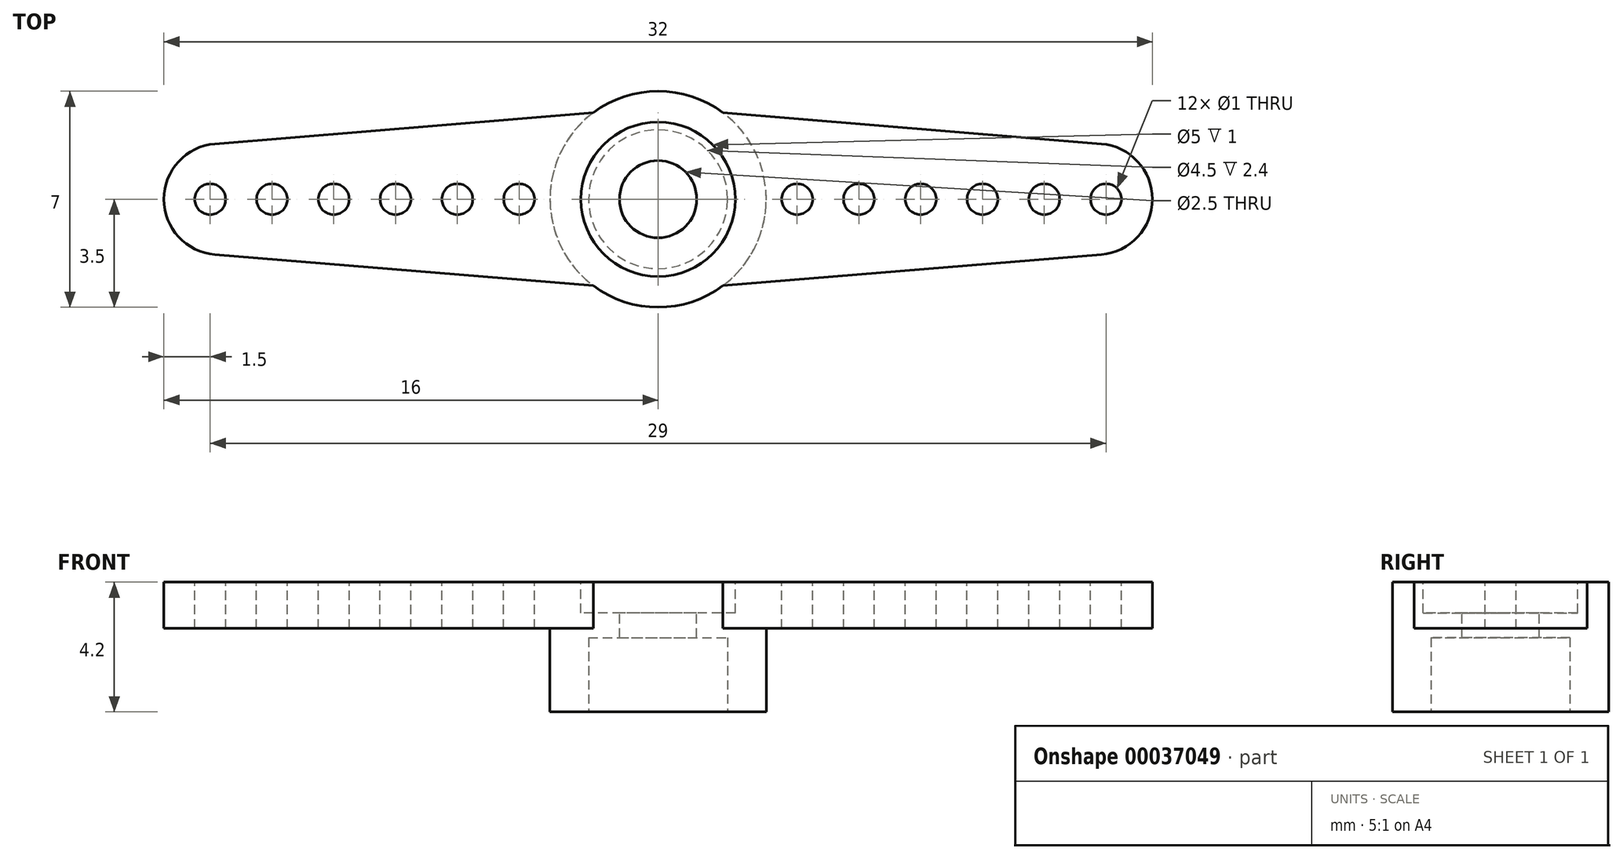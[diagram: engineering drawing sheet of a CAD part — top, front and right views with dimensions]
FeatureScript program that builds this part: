
annotation { "Feature Type Name" : "Feature", "Feature Type Description" : "" }
export const myFeature = defineFeature(function(context is Context, id is Id, definition is map)
    precondition{}
    {
        {
            var Q0;
            Q0=qCreatedBy(makeId("Top.planeOp"),FACE);
            var sketch = newSketch(context, id + "F0", { "sketchPlane" : qUnion([Q0])});
            skCircle(sketch, "E0", {"center": v(0, 0) * mm, "radius": 3.5 * mm});
            skCircle(sketch, "E1", {"center": v(0, 0) * mm, "radius": 16 * mm, "construction": true});
            skLineSegment(sketch, "E2", {"start": v(-16, 0) * mm, "end": v(16, 0) * mm, "construction": true});
            skArc(sketch, "E3", {"start": v(-14.35, 1.8) * mm, "mid": v(-16, 0) * mm, "end": v(-14.35, -1.8) * mm});
            skLineSegment(sketch, "E4", {"start": v(-14.35, 1.8) * mm, "end": v(-2.1, 2.8) * mm});
            skLineSegment(sketch, "E5.0.MirrorCS", {"start": v(-14.35, -1.8) * mm, "end": v(-2.1, -2.8) * mm});
            skLineSegment(sketch, "E6", {"start": v(0, 16) * mm, "end": v(0, -16) * mm, "construction": true});
            skLineSegment(sketch, "E7.0.MirrorCS", {"start": v(14.35, 1.8) * mm, "end": v(2.1, 2.8) * mm});
            skArc(sketch, "E8.0.MirrorCS", {"start": v(14.35, 1.8) * mm, "mid": v(16, 0) * mm, "end": v(14.35, -1.8) * mm});
            skLineSegment(sketch, "E9.0.MirrorCS", {"start": v(14.35, -1.8) * mm, "end": v(2.1, -2.8) * mm});
            skSolve(sketch);
        }
        {
            var Q0;
            {var subQ0=sQuery(id+"F0.wireOp",EDGE,"E0");var subQ4=makeQuery(id+"F0.imprint","INTERSECT",VERTEX,{"derivedFrom":[subQ0,sQuery(id+"F0.wireOp",EDGE,"E4")]});Q0=makeQuery(id+"F0.imprint","IMPRINT",FACE,{"disambiguationData":[TD([[makeQuery(id+"F0.imprint","IMPRINT",EDGE,{"disambiguationData":[TD([[subQ4,1.0]])],"derivedFrom":subQ0}),1.0]])]});}
            extrude(context, id + "F1", {"entities" : qUnion([Q0]), "depth" : 4.2 * mm});
        }
        {
            var Q0;
            Q0=makeQuery(id+"F1.opExtrude","CAP_FACE",FACE,{"disambiguationData":[OSD([sQuery(id+"F0.wireOp",EDGE,"E0")])],"isStart":false});
            var sketch = newSketch(context, id + "F2", { "sketchPlane" : qUnion([Q0])});
            skLineSegment(sketch, "E10.0", {"start": v(-14.35, 1.8) * mm, "end": v(-2.1, 2.8) * mm});
            skArc(sketch, "E11.0", {"start": v(-14.35, 1.8) * mm, "mid": v(-16, 0) * mm, "end": v(-14.35, -1.8) * mm});
            skLineSegment(sketch, "E12.0", {"start": v(-14.35, -1.8) * mm, "end": v(-2.1, -2.8) * mm});
            skLineSegment(sketch, "E13.0", {"start": v(14.35, -1.8) * mm, "end": v(2.1, -2.8) * mm});
            skArc(sketch, "E14.0", {"start": v(14.35, 1.8) * mm, "mid": v(16, 0) * mm, "end": v(14.35, -1.8) * mm});
            skLineSegment(sketch, "E15.0", {"start": v(14.35, 1.8) * mm, "end": v(2.1, 2.8) * mm});
            skArc(sketch, "E16.0", {"start": v(-2.1, 2.8) * mm, "mid": v(-3.5, 0) * mm, "end": v(-2.1, -2.8) * mm});
            skArc(sketch, "E17.trimOffspring", {"start": v(2.1, -2.8) * mm, "mid": v(3.5, 0) * mm, "end": v(2.1, 2.8) * mm});
            skLineSegment(sketch, "E18", {"start": v(-16, 0) * mm, "end": v(16, 0) * mm, "construction": true});
            skCircle(sketch, "E19", {"center": v(-14.5, 0) * mm, "radius": 0.5 * mm});
            skLineSegment(sketch, "E20", {"start": v(0, 4.57) * mm, "end": v(0, -5.46) * mm, "construction": true});
            skCircle(sketch, "E21.0.MirrorC", {"center": v(14.5, 0) * mm, "radius": 0.5 * mm});
            skCircle(sketch, "E22.1.0.0", {"center": v(-12.5, 0) * mm, "radius": 0.5 * mm});
            skCircle(sketch, "E22.2.0.0", {"center": v(-10.5, 0) * mm, "radius": 0.5 * mm});
            skCircle(sketch, "E22.3.0.0", {"center": v(-8.5, 0) * mm, "radius": 0.5 * mm});
            skCircle(sketch, "E22.4.0.0", {"center": v(-6.5, 0) * mm, "radius": 0.5 * mm});
            skCircle(sketch, "E22.5.0.0", {"center": v(-4.5, 0) * mm, "radius": 0.5 * mm});
            skLineSegment(sketch, "E22.direction1", {"start": v(-14.5, 0) * mm, "end": v(-12.5, 0) * mm, "construction": true});
            skCircle(sketch, "E23.0.MirrorC", {"center": v(4.5, 0) * mm, "radius": 0.5 * mm});
            skCircle(sketch, "E24.0.MirrorC", {"center": v(6.5, 0) * mm, "radius": 0.5 * mm});
            skCircle(sketch, "E25.0.MirrorC", {"center": v(8.5, 0) * mm, "radius": 0.5 * mm});
            skCircle(sketch, "E26.0.MirrorC", {"center": v(10.5, 0) * mm, "radius": 0.5 * mm});
            skCircle(sketch, "E27.0.MirrorC", {"center": v(12.5, 0) * mm, "radius": 0.5 * mm});
            skSolve(sketch);
        }
        {
            var Q0;
            Q0=qSketchRegion(id+"F2",true);
            extrude(context, id + "F3", {"entities" : qUnion([Q0]), "operationType" : NewBodyOperationType.ADD, "oppositeDirection" : true, "depth" : 1.5 * mm});
        }
        {
            var Q0;
            Q0=makeQuery(id+"F3.boolean.opBoolean","MERGE",FACE,{"derivedFrom":[makeQuery(id+"F1.opExtrude","CAP_FACE",FACE,{"disambiguationData":[OSD([sQuery(id+"F0.wireOp",EDGE,"E0")])],"isStart":false}),makeQuery(id+"F3.opExtrude","CAP_FACE",FACE,{"disambiguationData":[OSD([sQuery(id+"F2.wireOp",EDGE,"E10.0"),sQuery(id+"F2.wireOp",EDGE,"E11.0"),sQuery(id+"F2.wireOp",EDGE,"E12.0"),sQuery(id+"F2.wireOp",EDGE,"E16.0"),sQuery(id+"F2.wireOp",EDGE,"E19"),sQuery(id+"F2.wireOp",EDGE,"E22.1.0.0"),sQuery(id+"F2.wireOp",EDGE,"E22.2.0.0"),sQuery(id+"F2.wireOp",EDGE,"E22.3.0.0"),sQuery(id+"F2.wireOp",EDGE,"E22.4.0.0"),sQuery(id+"F2.wireOp",EDGE,"E22.5.0.0")])],"isStart":true}),makeQuery(id+"F3.opExtrude","CAP_FACE",FACE,{"disambiguationData":[OSD([sQuery(id+"F2.wireOp",EDGE,"E13.0"),sQuery(id+"F2.wireOp",EDGE,"E14.0"),sQuery(id+"F2.wireOp",EDGE,"E15.0"),sQuery(id+"F2.wireOp",EDGE,"E17.trimOffspring"),sQuery(id+"F2.wireOp",EDGE,"E21.0.MirrorC"),sQuery(id+"F2.wireOp",EDGE,"E23.0.MirrorC"),sQuery(id+"F2.wireOp",EDGE,"E24.0.MirrorC"),sQuery(id+"F2.wireOp",EDGE,"E25.0.MirrorC"),sQuery(id+"F2.wireOp",EDGE,"E26.0.MirrorC"),sQuery(id+"F2.wireOp",EDGE,"E27.0.MirrorC")])],"isStart":true})]});
            var sketch = newSketch(context, id + "F4", { "sketchPlane" : qUnion([Q0])});
            skCircle(sketch, "E28", {"center": v(0, 0) * mm, "radius": 2.5 * mm});
            skSolve(sketch);
        }
        {
            var Q0;
            Q0=qSketchRegion(id+"F4",true);
            extrude(context, id + "F5", {"entities" : qUnion([Q0]), "operationType" : NewBodyOperationType.REMOVE, "oppositeDirection" : true, "depth" : 1 * mm});
        }
        {
            var Q0;
            Q0=makeQuery(id+"F1.opExtrude","CAP_FACE",FACE,{"disambiguationData":[OSD([sQuery(id+"F0.wireOp",EDGE,"E0")])],"isStart":true});
            var sketch = newSketch(context, id + "F6", { "sketchPlane" : qUnion([Q0])});
            skCircle(sketch, "E29", {"center": v(0, 0) * mm, "radius": 2.25 * mm});
            skSolve(sketch);
        }
        {
            var Q0;
            Q0=qSketchRegion(id+"F6",true);
            extrude(context, id + "F7", {"entities" : qUnion([Q0]), "operationType" : NewBodyOperationType.REMOVE, "oppositeDirection" : true, "depth" : 2.4 * mm});
        }
        {
            var Q0;
            Q0=makeQuery(id+"F5.boolean.opBoolean","COPY",FACE,{"derivedFrom":makeQuery(id+"F5.opExtrude","CAP_FACE",FACE,{"disambiguationData":[OSD([sQuery(id+"F4.wireOp",EDGE,"E28")])],"isStart":false})});
            var sketch = newSketch(context, id + "F8", { "sketchPlane" : qUnion([Q0])});
            skCircle(sketch, "E30", {"center": v(0, 0) * mm, "radius": 1.25 * mm});
            skSolve(sketch);
        }
        {
            var Q0;
            Q0=qSketchRegion(id+"F8",true);
            extrude(context, id + "F9", {"entities" : qUnion([Q0]), "operationType" : NewBodyOperationType.REMOVE, "oppositeDirection" : true, "depth" : 25 * mm});
        }
    });
